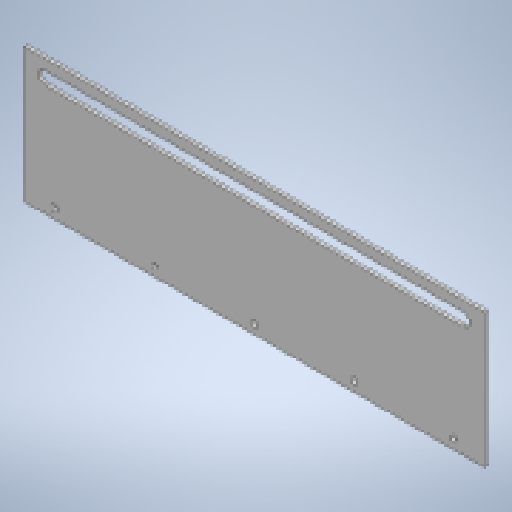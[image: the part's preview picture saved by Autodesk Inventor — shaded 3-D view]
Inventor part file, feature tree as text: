
AUTODESK INVENTOR PART (.ipt)
format: ipt  version: 2024 (Build 280153000, 153)  size: 238,592 bytes
history: native  units: mm
features: other x9, reference x7, extrude x4, sketch x4, chamfer x1, fillet x1
ambient origin geometry x8: Origin, YZ Plane, XZ Plane, XY Plane, X Axis, Y Axis, Z Axis, Center Point
bodies: Body1 (feature_tree)
feature tree (26):
  other  "ソリッド1"
  extrude  "押し出し1"  Depth=3.2mm
  extrude  "押し出し2"  Depth=3.2mm
  extrude  "押し出し3"  Depth=3.2mm
  chamfer  "面取り1"  Distance=3.2mm
  extrude  "押し出し6"  Depth=3.2mm
  fillet  "フィレット2"  Radius=6.0mm
  sketch  "スケッチ1"
  reference  "参照1"
  reference  "参照2"
  reference  "参照3"
  sketch  "スケッチ2"
  sketch  "スケッチ3"
  reference  "参照4"
  reference  "参照5"
  reference  "参照6"
  sketch  "スケッチ6"
  reference  "参照14"
  other  "<userpath>\OneDrive\ドキュメント\Inventor\Vixen\leg.iam"
  other  "leg.iam"
  other  "SR4-500_On:1"
  other  "KRS2500_scale:1"
  other  "平歯車:1"
  other  "平歯車1:1"
  other  "wall2:1"
  other  "02157_SmallDiameterHornB:3"
